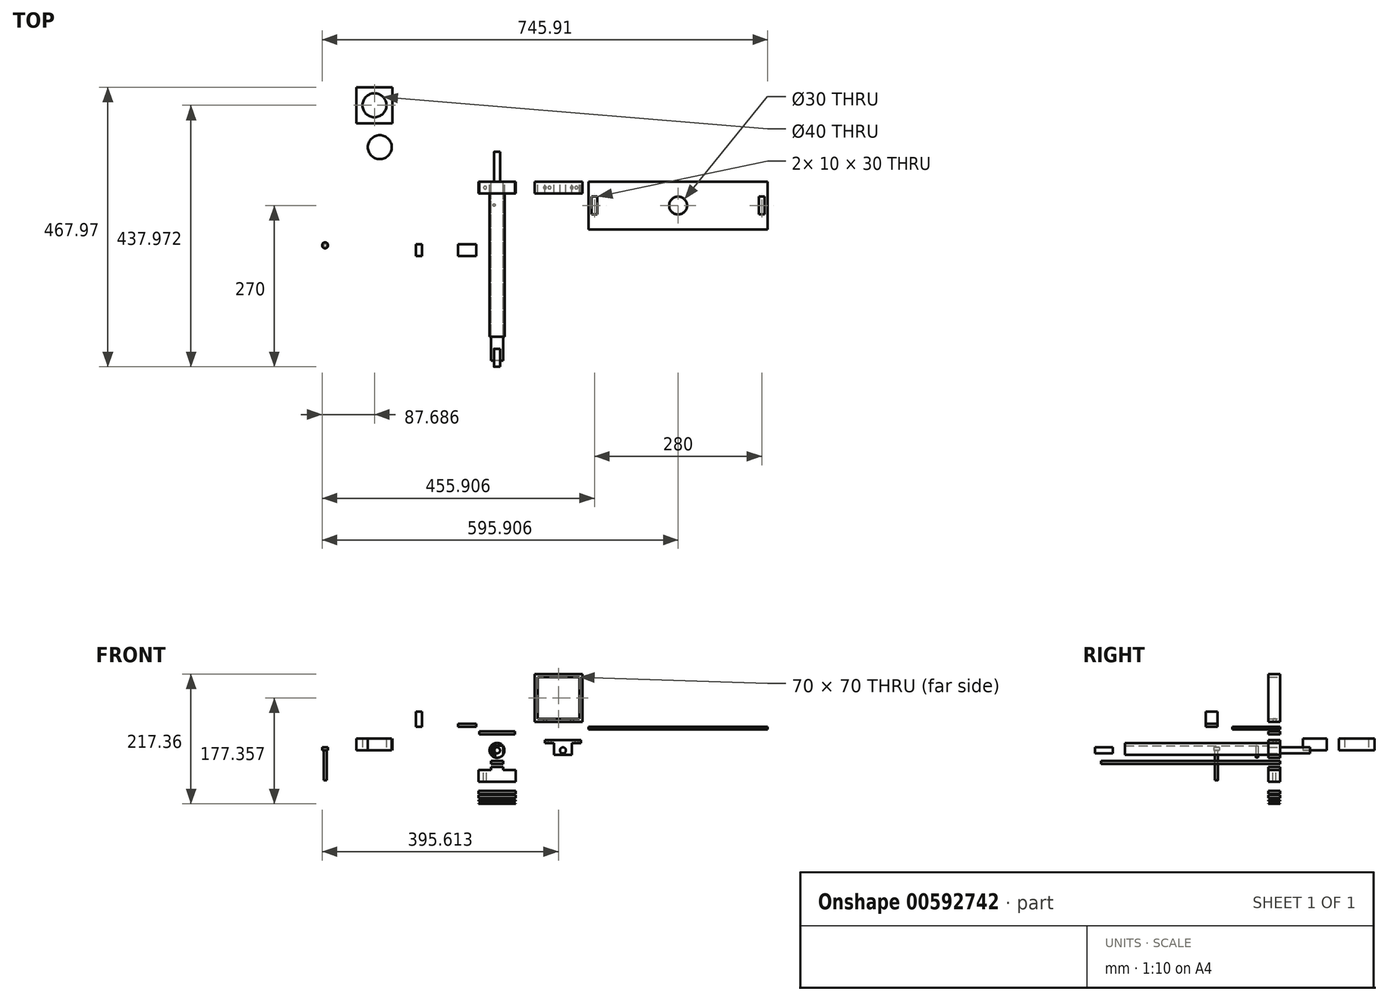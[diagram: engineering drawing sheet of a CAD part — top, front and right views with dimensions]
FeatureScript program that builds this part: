
annotation { "Feature Type Name" : "Feature", "Feature Type Description" : "" }
export const myFeature = defineFeature(function(context is Context, id is Id, definition is map)
    precondition{}
    {
        {
            var Q0;
            Q0=qCreatedBy(makeId("Front.planeOp"),FACE);
            var sketch = newSketch(context, id + "F0", { "sketchPlane" : qUnion([Q0])});
            skCircle(sketch, "E0", {"center": v(0, 0) * mm, "radius": 12.5 * mm});
            skCircle(sketch, "E1", {"center": v(110.3, 0) * mm, "radius": 5 * mm});
            skLineSegment(sketch, "E2.bottom", {"start": v(-30, 31.74) * mm, "end": v(30, 31.74) * mm});
            skLineSegment(sketch, "E2.top", {"start": v(-30, 26.74) * mm, "end": v(30, 26.74) * mm});
            skLineSegment(sketch, "E2.left", {"start": v(-30, 31.74) * mm, "end": v(-30, 26.74) * mm});
            skLineSegment(sketch, "E2.right", {"start": v(30, 31.74) * mm, "end": v(30, 26.74) * mm});
            skPoint(sketch, "E2.middle", {"position": v(0, 29.24) * mm});
            skLineSegment(sketch, "E3", {"start": v(110.3, 10) * mm, "end": v(110.3, -10) * mm, "construction": true});
            skCircle(sketch, "E4", {"center": v(110.3, 0) * mm, "radius": 12.5 * mm, "construction": true});
            skLineSegment(sketch, "E5", {"start": v(97.8, 0) * mm, "end": v(122.8, 0) * mm, "construction": true});
            skLineSegment(sketch, "E6", {"start": v(110.3, 12.5) * mm, "end": v(79.29, 12.5) * mm, "construction": true});
            skLineSegment(sketch, "E7", {"start": v(110.3, 5) * mm, "end": v(79.29, 5) * mm, "construction": true});
            skLineSegment(sketch, "E8", {"start": v(110.3, -5) * mm, "end": v(79.29, -5) * mm, "construction": true});
            skLineSegment(sketch, "E9", {"start": v(110.3, -12.5) * mm, "end": v(79.29, -12.5) * mm, "construction": true});
            skLineSegment(sketch, "E10", {"start": v(110.3, -7.5) * mm, "end": v(125.3, -7.5) * mm});
            skLineSegment(sketch, "E11", {"start": v(110.3, 17.5) * mm, "end": v(140.3, 17.5) * mm});
            skLineSegment(sketch, "E12", {"start": v(125.3, 12.5) * mm, "end": v(140.3, 12.5) * mm});
            skLineSegment(sketch, "E13", {"start": v(125.3, -7.5) * mm, "end": v(125.3, 12.5) * mm});
            skLineSegment(sketch, "E14", {"start": v(140.3, 17.5) * mm, "end": v(140.3, 12.5) * mm});
            skPoint(sketch, "E15.orphan", {"position": v(110.3, 12.5) * mm});
            skLineSegment(sketch, "E16.MirrorCS", {"start": v(95.3, 12.5) * mm, "end": v(80.3, 12.5) * mm});
            skLineSegment(sketch, "E17.MirrorCS", {"start": v(80.3, 17.5) * mm, "end": v(80.3, 12.5) * mm});
            skLineSegment(sketch, "E18.MirrorCS", {"start": v(110.3, 17.5) * mm, "end": v(80.3, 17.5) * mm});
            skLineSegment(sketch, "E19.MirrorCS", {"start": v(95.3, -7.5) * mm, "end": v(95.3, 12.5) * mm});
            skLineSegment(sketch, "E20.MirrorCS", {"start": v(110.3, -7.5) * mm, "end": v(95.3, -7.5) * mm});
            skLineSegment(sketch, "E21.top", {"start": v(0, -27.58) * mm, "end": v(10, -27.58) * mm});
            skLineSegment(sketch, "E22", {"start": v(10.93, -32.58) * mm, "end": v(30.93, -32.58) * mm});
            skLineSegment(sketch, "E23", {"start": v(30.93, -32.58) * mm, "end": v(30.93, -52.58) * mm});
            skLineSegment(sketch, "E24", {"start": v(30.93, -52.58) * mm, "end": v(0, -52.58) * mm});
            skLineSegment(sketch, "E25.MirrorCS", {"start": v(0, -27.58) * mm, "end": v(-10, -27.58) * mm});
            skLineSegment(sketch, "E26.MirrorCS", {"start": v(-10.93, -32.58) * mm, "end": v(-30.93, -32.58) * mm});
            skLineSegment(sketch, "E27.MirrorCS", {"start": v(-30.93, -32.58) * mm, "end": v(-30.93, -52.58) * mm});
            skLineSegment(sketch, "E28.MirrorCS", {"start": v(-30.93, -52.58) * mm, "end": v(0, -52.58) * mm});
            skLineSegment(sketch, "E29", {"start": v(0, -22.52) * mm, "end": v(10, -22.52) * mm});
            skLineSegment(sketch, "E30", {"start": v(10, -22.52) * mm, "end": v(10, -17.52) * mm});
            skLineSegment(sketch, "E31", {"start": v(10, -17.52) * mm, "end": v(0, -17.52) * mm});
            skLineSegment(sketch, "E32.MirrorCS", {"start": v(-10, -17.52) * mm, "end": v(0, -17.52) * mm});
            skLineSegment(sketch, "E33.MirrorCS", {"start": v(0, -22.52) * mm, "end": v(-10, -22.52) * mm});
            skLineSegment(sketch, "E34.MirrorCS", {"start": v(-10, -22.52) * mm, "end": v(-10, -17.52) * mm});
            skLineSegment(sketch, "E35.bottom", {"start": v(137.73, 52.7) * mm, "end": v(67.73, 52.7) * mm});
            skLineSegment(sketch, "E35.top", {"start": v(137.73, 122.7) * mm, "end": v(67.73, 122.7) * mm});
            skLineSegment(sketch, "E35.left", {"start": v(137.73, 52.7) * mm, "end": v(137.73, 122.7) * mm});
            skLineSegment(sketch, "E35.right", {"start": v(67.73, 52.7) * mm, "end": v(67.73, 122.7) * mm});
            skPoint(sketch, "E35.middle", {"position": v(102.73, 87.7) * mm});
            skLineSegment(sketch, "E36.bottom", {"start": v(62.73, 127.7) * mm, "end": v(142.73, 127.7) * mm});
            skLineSegment(sketch, "E36.top", {"start": v(62.73, 47.7) * mm, "end": v(142.73, 47.7) * mm});
            skLineSegment(sketch, "E36.left", {"start": v(62.73, 127.7) * mm, "end": v(62.73, 47.7) * mm});
            skLineSegment(sketch, "E36.right", {"start": v(142.73, 127.7) * mm, "end": v(142.73, 47.7) * mm});
            skLineSegment(sketch, "E37.bottom", {"start": v(-30.93, -79.86) * mm, "end": v(30.93, -79.86) * mm});
            skLineSegment(sketch, "E37.top", {"start": v(-30.93, -74.86) * mm, "end": v(30.93, -74.86) * mm});
            skLineSegment(sketch, "E37.left", {"start": v(-30.93, -79.86) * mm, "end": v(-30.93, -74.86) * mm});
            skLineSegment(sketch, "E37.right", {"start": v(30.93, -79.86) * mm, "end": v(30.93, -74.86) * mm});
            skLineSegment(sketch, "E38.MirrorCS", {"start": v(-30.74, -88.65) * mm, "end": v(31.12, -88.65) * mm});
            skLineSegment(sketch, "E39.MirrorCS", {"start": v(-30.74, -89.65) * mm, "end": v(31.12, -89.65) * mm});
            skLineSegment(sketch, "E40", {"start": v(-30.93, -82.76) * mm, "end": v(30.93, -82.76) * mm});
            skLineSegment(sketch, "E41", {"start": v(30.93, -82.76) * mm, "end": v(30.93, -84.76) * mm});
            skLineSegment(sketch, "E42", {"start": v(30.93, -84.76) * mm, "end": v(-30.93, -84.76) * mm});
            skLineSegment(sketch, "E43", {"start": v(-30.93, -84.76) * mm, "end": v(-30.93, -82.76) * mm});
            skLineSegment(sketch, "E44", {"start": v(-30.74, -88.65) * mm, "end": v(-30.74, -89.65) * mm});
            skLineSegment(sketch, "E45", {"start": v(31.12, -88.65) * mm, "end": v(31.12, -89.65) * mm});
            skLineSegment(sketch, "E46", {"start": v(-30.93, -72.74) * mm, "end": v(30.93, -72.74) * mm});
            skLineSegment(sketch, "E47", {"start": v(30.93, -72.74) * mm, "end": v(30.93, -67.74) * mm});
            skLineSegment(sketch, "E48", {"start": v(30.93, -67.74) * mm, "end": v(-30.93, -67.74) * mm});
            skLineSegment(sketch, "E49", {"start": v(-30.93, -67.74) * mm, "end": v(-30.93, -72.74) * mm});
            skLineSegment(sketch, "E50", {"start": v(-10, -27.58) * mm, "end": v(-10, -32.58) * mm});
            skLineSegment(sketch, "E51", {"start": v(-10, -32.58) * mm, "end": v(-10.93, -32.58) * mm});
            skPoint(sketch, "E52.MirrorCS.end.orphan", {"position": v(-10, -27.58) * mm});
            skPoint(sketch, "E52.MirrorCS.start.orphan", {"position": v(-10.93, -32.58) * mm});
            skLineSegment(sketch, "E53", {"start": v(10, -27.58) * mm, "end": v(10, -32.58) * mm});
            skLineSegment(sketch, "E54", {"start": v(10, -32.58) * mm, "end": v(10.93, -32.58) * mm});
            skLineSegment(sketch, "E55.left", {"start": v(194.47, 95.4) * mm, "end": v(194.47, 97.9) * mm});
            skLineSegment(sketch, "E56.bottom", {"start": v(-122.7, 157) * mm, "end": v(-422.7, 157) * mm});
            skLineSegment(sketch, "E56.top", {"start": v(-122.7, 159.5) * mm, "end": v(-422.7, 159.5) * mm});
            skLineSegment(sketch, "E56.left", {"start": v(-122.7, 157) * mm, "end": v(-122.7, 159.5) * mm});
            skLineSegment(sketch, "E56.right", {"start": v(-422.7, 157) * mm, "end": v(-422.7, 159.5) * mm});
            skLineSegment(sketch, "E57", {"start": v(-272.7, 150) * mm, "end": v(-272.7, 153.49) * mm, "construction": true});
            skPoint(sketch, "E57.startSnap0", {"position": v(-272.7, 157) * mm});
            skSolve(sketch);
        }
        {
            var Q0;
            Q0=makeQuery(id+"F0.imprint","IMPRINT",FACE,{"disambiguationData":[TD([[makeQuery(id+"F0.imprint","IMPRINT",EDGE,{"derivedFrom":sQuery(id+"F0.wireOp",EDGE,"E1")}),-1.0]])]});
            var Q1;
            Q1=makeQuery(id+"F0.imprint","IMPRINT",FACE,{"disambiguationData":[TD([[makeQuery(id+"F0.imprint","IMPRINT",EDGE,{"derivedFrom":sQuery(id+"F0.wireOp",EDGE,"E2.bottom")}),-1.0]])]});
            var Q2;
            Q2=makeQuery(id+"F0.imprint","IMPRINT",FACE,{"disambiguationData":[TD([[makeQuery(id+"F0.imprint","IMPRINT",EDGE,{"derivedFrom":sQuery(id+"F0.wireOp",EDGE,"E21.top")}),-1.0]])]});
            var Q3;
            Q3=makeQuery(id+"F0.imprint","IMPRINT",FACE,{"disambiguationData":[TD([[makeQuery(id+"F0.imprint","IMPRINT",EDGE,{"derivedFrom":sQuery(id+"F0.wireOp",EDGE,"E35.bottom")}),1.0]])]});
            var Q4;
            Q4=makeQuery(id+"F0.imprint","IMPRINT",FACE,{"disambiguationData":[TD([[makeQuery(id+"F0.imprint","IMPRINT",EDGE,{"derivedFrom":sQuery(id+"F0.wireOp",EDGE,"E37.bottom")}),1.0]])]});
            var Q5;
            Q5=makeQuery(id+"F0.imprint","IMPRINT",FACE,{"disambiguationData":[TD([[makeQuery(id+"F0.imprint","IMPRINT",EDGE,{"derivedFrom":sQuery(id+"F0.wireOp",EDGE,"E38.MirrorCS")}),-1.0]])]});
            var Q6;
            Q6=makeQuery(id+"F0.imprint","IMPRINT",FACE,{"disambiguationData":[TD([[makeQuery(id+"F0.imprint","IMPRINT",EDGE,{"derivedFrom":sQuery(id+"F0.wireOp",EDGE,"E40")}),-1.0]])]});
            var Q7;
            Q7=makeQuery(id+"F0.imprint","IMPRINT",FACE,{"disambiguationData":[TD([[makeQuery(id+"F0.imprint","IMPRINT",EDGE,{"derivedFrom":sQuery(id+"F0.wireOp",EDGE,"E46")}),1.0]])]});
            var Q8;
            {var subQ5=sQuery(id+"F0.wireOp",EDGE,"E55.right");Q8=makeQuery(id+"F0.imprint","IMPRINT",FACE,{"disambiguationData":[TD([[makeQuery(id+"F0.imprint","IMPRINT",EDGE,{"derivedFrom":subQ5}),-1.0]])]});}
            extrude(context, id + "F1", {"entities" : qUnion([Q0, Q1, Q2, Q3, Q4, Q5, Q6, Q7, Q8]), "depth" : 20 * mm, "offsetDistance" : 25 * mm});
        }
        {
            var Q0;
            Q0=makeQuery(id+"F0.imprint","IMPRINT",FACE,{"disambiguationData":[TD([[makeQuery(id+"F0.imprint","IMPRINT",EDGE,{"derivedFrom":sQuery(id+"F0.wireOp",EDGE,"E0")}),1.0]])]});
            extrude(context, id + "F2", {"entities" : qUnion([Q0]), "depth" : 260 * mm, "offsetDistance" : 25 * mm});
        }
        {
            var Q0;
            Q0=makeQuery(id+"F2.opExtrude","CAP_FACE",FACE,{"disambiguationData":[OSD([sQuery(id+"F0.wireOp",EDGE,"E0")])],"isStart":false});
            var sketch = newSketch(context, id + "F3", { "sketchPlane" : qUnion([Q0])});
            skCircle(sketch, "E58", {"center": v(0, 0) * mm, "radius": 5 * mm});
            skSolve(sketch);
        }
        {
            var Q0;
            Q0=makeQuery(id+"F3.imprint","IMPRINT",FACE,{"disambiguationData":[TD([[makeQuery(id+"F3.imprint","IMPRINT",EDGE,{"derivedFrom":sQuery(id+"F3.wireOp",EDGE,"E58")}),1.0]])]});
            extrude(context, id + "F4", {"entities" : qUnion([Q0]), "operationType" : NewBodyOperationType.ADD, "depth" : 50 * mm, "offsetDistance" : 25 * mm});
        }
        {
            var Q0;
            Q0=makeQuery(id+"F0.imprint","IMPRINT",FACE,{"disambiguationData":[TD([[makeQuery(id+"F0.imprint","IMPRINT",EDGE,{"derivedFrom":sQuery(id+"F0.wireOp",EDGE,"E29")}),1.0]])]});
            extrude(context, id + "F5", {"entities" : qUnion([Q0]), "depth" : 300 * mm, "offsetDistance" : 25 * mm});
        }
        {
            var Q0;
            Q0=makeQuery(id+"F1.opExtrude","SWEPT_FACE",FACE,{"disambiguationData":[OSD([sQuery(id+"F0.wireOp",EDGE,"E26.MirrorCS")])]});
            var sketch = newSketch(context, id + "F6", { "sketchPlane" : qUnion([Q0])});
            skCircle(sketch, "E59", {"center": v(-20, -10) * mm, "radius": 2.5 * mm});
            skSolve(sketch);
        }
        {
            var Q0;
            Q0=makeQuery(id+"F6.imprint","IMPRINT",FACE,{"disambiguationData":[TD([[makeQuery(id+"F6.imprint","IMPRINT",EDGE,{"derivedFrom":sQuery(id+"F6.wireOp",EDGE,"E59")}),1.0]])]});
            var Q1;
            Q1=makeQuery(id+"FNYWGUJzlf6PVvf_4.imprint","IMPRINT",FACE,{"disambiguationData":[TD([[makeQuery(id+"FNYWGUJzlf6PVvf_4.imprint","IMPRINT",EDGE,{"derivedFrom":sQuery(id+"FNYWGUJzlf6PVvf_4.wireOp",EDGE,"JrdPBHnR-5tIZ-cZ5f-IPz8-CMVoVNEgzM20")}),1.0]])]});
            extrude(context, id + "F7", {"entities" : qUnion([Q0, Q1]), "operationType" : NewBodyOperationType.REMOVE, "oppositeDirection" : true, "depth" : 25 * mm, "offsetDistance" : 25 * mm});
        }
        {
            var Q0;
            Q0=makeQuery(id+"F1.opExtrude","SWEPT_FACE",FACE,{"disambiguationData":[OSD([sQuery(id+"F0.wireOp",EDGE,"E12")])]});
            var sketch = newSketch(context, id + "F8", { "sketchPlane" : qUnion([Q0])});
            skCircle(sketch, "E60", {"center": v(132.8, 10) * mm, "radius": 2.5 * mm});
            skPoint(sketch, "E60.centerSnap0", {"position": v(132.8, 20) * mm});
            skPoint(sketch, "E60.centerSnap1", {"position": v(125.3, 10) * mm});
            skSolve(sketch);
        }
        {
            var Q0;
            Q0=makeQuery(id+"F1.opExtrude","SWEPT_FACE",FACE,{"disambiguationData":[OSD([sQuery(id+"F0.wireOp",EDGE,"E16.MirrorCS")])]});
            var sketch = newSketch(context, id + "F9", { "sketchPlane" : qUnion([Q0])});
            skCircle(sketch, "E61", {"center": v(87.8, 10) * mm, "radius": 2.5 * mm});
            skPoint(sketch, "E61.centerSnap0", {"position": v(80.3, 10) * mm});
            skPoint(sketch, "E61.centerSnap1", {"position": v(87.8, 20) * mm});
            skSolve(sketch);
        }
        {
            var Q0;
            Q0=makeQuery(id+"F9.imprint","IMPRINT",FACE,{"disambiguationData":[TD([[makeQuery(id+"F9.imprint","IMPRINT",EDGE,{"derivedFrom":sQuery(id+"F9.wireOp",EDGE,"E61")}),1.0]])]});
            var Q1;
            Q1=makeQuery(id+"F8.imprint","IMPRINT",FACE,{"disambiguationData":[TD([[makeQuery(id+"F8.imprint","IMPRINT",EDGE,{"derivedFrom":sQuery(id+"F8.wireOp",EDGE,"E60")}),1.0]])]});
            extrude(context, id + "F10", {"entities" : qUnion([Q0, Q1]), "operationType" : NewBodyOperationType.REMOVE, "oppositeDirection" : true, "depth" : 25 * mm, "offsetDistance" : 25 * mm});
        }
        {
            var Q0;
            Q0=makeQuery(id+"F5.opExtrude","SWEPT_FACE",FACE,{"disambiguationData":[OSD([sQuery(id+"F0.wireOp",EDGE,"E31"),sQuery(id+"F0.wireOp",EDGE,"E32.MirrorCS")])]});
            var sketch = newSketch(context, id + "F11", { "sketchPlane" : qUnion([Q0])});
            skLineSegment(sketch, "E62", {"start": v(-10, -280) * mm, "end": v(10, -280) * mm});
            skCircle(sketch, "E63", {"center": v(5, -39.13) * mm, "radius": 1.93 * mm});
            skPoint(sketch, "E64.orphan", {"position": v(0, -300) * mm});
            skCircle(sketch, "E65.MirrorC", {"center": v(-5, -39.13) * mm, "radius": 1.93 * mm});
            skLineSegment(sketch, "E66", {"start": v(10, -20) * mm, "end": v(-10, -20) * mm});
            skSolve(sketch);
        }
        {
            var Q0;
            Q0=makeQuery(id+"F11.imprint","IMPRINT",FACE,{"disambiguationData":[TD([[makeQuery(id+"F11.imprint","IMPRINT",EDGE,{"derivedFrom":sQuery(id+"F11.wireOp",EDGE,"E65.MirrorC")}),-1.0]])]});
            var Q1;
            Q1=makeQuery(id+"F11.imprint","IMPRINT",FACE,{"disambiguationData":[TD([[makeQuery(id+"F11.imprint","IMPRINT",EDGE,{"derivedFrom":sQuery(id+"F11.wireOp",EDGE,"E63")}),1.0]])]});
            extrude(context, id + "F12", {"entities" : qUnion([Q0, Q1]), "operationType" : NewBodyOperationType.REMOVE, "depth" : 25 * mm, "offsetDistance" : 25 * mm});
        }
        {
            var Q0;
            Q0=makeQuery(id+"F1.opExtrude","SWEPT_FACE",FACE,{"disambiguationData":[OSD([sQuery(id+"F0.wireOp",EDGE,"E36.top")])]});
            var sketch = newSketch(context, id + "F13", { "sketchPlane" : qUnion([Q0])});
            skCircle(sketch, "E67", {"center": v(80.23, 10) * mm, "radius": 2.5 * mm});
            skCircle(sketch, "E68", {"center": v(125.23, 10) * mm, "radius": 2.5 * mm});
            skLineSegment(sketch, "E69", {"start": v(62.73, 20) * mm, "end": v(142.73, 20) * mm, "construction": true});
            skLineSegment(sketch, "E70", {"start": v(142.73, 20) * mm, "end": v(142.73, 0) * mm, "construction": true});
            skLineSegment(sketch, "E71", {"start": v(142.73, 0) * mm, "end": v(62.73, 0) * mm, "construction": true});
            skLineSegment(sketch, "E72", {"start": v(62.73, 0) * mm, "end": v(62.73, 20) * mm, "construction": true});
            skLineSegment(sketch, "E73", {"start": v(67.73, 20) * mm, "end": v(67.73, 0) * mm, "construction": true});
            skLineSegment(sketch, "E74", {"start": v(137.73, 20) * mm, "end": v(137.73, 0) * mm, "construction": true});
            skSolve(sketch);
        }
        {
            var Q0;
            Q0=makeQuery(id+"F2.opExtrude","CAP_FACE",FACE,{"disambiguationData":[OSD([sQuery(id+"F0.wireOp",EDGE,"E0")])],"isStart":true});
            var sketch = newSketch(context, id + "F14", { "sketchPlane" : qUnion([Q0])});
            skCircle(sketch, "E75", {"center": v(0, 0) * mm, "radius": 5 * mm});
            skSolve(sketch);
        }
        {
            var Q0;
            Q0=qSketchRegion(id+"F14",true);
            extrude(context, id + "F15", {"entities" : qUnion([Q0]), "operationType" : NewBodyOperationType.ADD, "depth" : 50 * mm, "offsetDistance" : 25 * mm});
        }
        {
            var Q0;
            Q0=qCreatedBy(makeId("Front.planeOp"),FACE);
            var sketch = newSketch(context, id + "F16", { "sketchPlane" : qUnion([Q0])});
            skLineSegment(sketch, "E76.bottom", {"start": v(153.03, 39.78) * mm, "end": v(453.03, 39.78) * mm});
            skLineSegment(sketch, "E76.top", {"start": v(153.03, 34.78) * mm, "end": v(453.03, 34.78) * mm});
            skLineSegment(sketch, "E76.left", {"start": v(153.03, 39.78) * mm, "end": v(153.03, 34.78) * mm});
            skLineSegment(sketch, "E76.right", {"start": v(453.03, 39.78) * mm, "end": v(453.03, 34.78) * mm});
            skSolve(sketch);
        }
        {
            var Q0;
            Q0=makeQuery(id+"F16.imprint","IMPRINT",FACE,{"disambiguationData":[TD([[makeQuery(id+"F16.imprint","IMPRINT",EDGE,{"derivedFrom":sQuery(id+"F16.wireOp",EDGE,"E76.bottom")}),-1.0]])]});
            extrude(context, id + "F17", {"entities" : qUnion([Q0]), "depth" : 80 * mm, "offsetDistance" : 25 * mm});
        }
        {
            var Q0;
            Q0=makeQuery(id+"F17.opExtrude","SWEPT_FACE",FACE,{"disambiguationData":[OSD([sQuery(id+"F16.wireOp",EDGE,"E76.bottom")])]});
            var sketch = newSketch(context, id + "F18", { "sketchPlane" : qUnion([Q0])});
            skLineSegment(sketch, "E77", {"start": v(173.03, 0) * mm, "end": v(173.03, -80) * mm});
            skLineSegment(sketch, "E78.bottom", {"start": v(158.03, -25) * mm, "end": v(168.03, -25) * mm});
            skLineSegment(sketch, "E78.top", {"start": v(158.03, -55) * mm, "end": v(168.03, -55) * mm});
            skLineSegment(sketch, "E78.left", {"start": v(158.03, -25) * mm, "end": v(158.03, -55) * mm});
            skLineSegment(sketch, "E78.right", {"start": v(168.03, -25) * mm, "end": v(168.03, -55) * mm});
            skPoint(sketch, "E78.middle", {"position": v(163.03, -40) * mm});
            skLineSegment(sketch, "E79", {"start": v(303.03, 0) * mm, "end": v(303.03, -80) * mm, "construction": true});
            skLineSegment(sketch, "E80.MirrorCS", {"start": v(438.03, -25) * mm, "end": v(438.03, -55) * mm});
            skLineSegment(sketch, "E81.MirrorCS", {"start": v(448.03, -25) * mm, "end": v(438.03, -25) * mm});
            skLineSegment(sketch, "E82.MirrorCS", {"start": v(448.03, -25) * mm, "end": v(448.03, -55) * mm});
            skLineSegment(sketch, "E83.MirrorCS", {"start": v(448.03, -55) * mm, "end": v(438.03, -55) * mm});
            skLineSegment(sketch, "E84.MirrorCS", {"start": v(433.03, 0) * mm, "end": v(433.03, -80) * mm});
            skLineSegment(sketch, "E85.bottom", {"start": v(-65.07, -104.85) * mm, "end": v(-35.07, -104.85) * mm});
            skLineSegment(sketch, "E85.top", {"start": v(-65.07, -124.85) * mm, "end": v(-35.07, -124.85) * mm});
            skLineSegment(sketch, "E85.left", {"start": v(-65.07, -104.85) * mm, "end": v(-65.07, -124.85) * mm});
            skLineSegment(sketch, "E85.right", {"start": v(-35.07, -104.85) * mm, "end": v(-35.07, -124.85) * mm});
            skLineSegment(sketch, "E86.bottom", {"start": v(-135.53, -104.85) * mm, "end": v(-125.53, -104.85) * mm});
            skLineSegment(sketch, "E86.top", {"start": v(-135.53, -124.85) * mm, "end": v(-125.53, -124.85) * mm});
            skLineSegment(sketch, "E86.left", {"start": v(-135.53, -104.85) * mm, "end": v(-135.53, -124.85) * mm});
            skLineSegment(sketch, "E86.right", {"start": v(-125.53, -104.85) * mm, "end": v(-125.53, -124.85) * mm});
            skCircle(sketch, "E87", {"center": v(303.03, -40) * mm, "radius": 15 * mm});
            skSolve(sketch);
        }
        {
            var Q0;
            Q0=qCreatedBy(makeId("Top.planeOp"),FACE);
            var sketch = newSketch(context, id + "F19", { "sketchPlane" : qUnion([Q0])});
            skCircle(sketch, "E88", {"center": v(-196.25, 57.8) * mm, "radius": 20 * mm});
            skLineSegment(sketch, "E89.bottom", {"start": v(-235.2, 97.97) * mm, "end": v(-175.2, 97.97) * mm});
            skLineSegment(sketch, "E89.top", {"start": v(-235.2, 157.97) * mm, "end": v(-175.2, 157.97) * mm});
            skLineSegment(sketch, "E89.left", {"start": v(-235.2, 97.97) * mm, "end": v(-235.2, 157.97) * mm});
            skLineSegment(sketch, "E89.right", {"start": v(-175.2, 97.97) * mm, "end": v(-175.2, 157.97) * mm});
            skCircle(sketch, "E90", {"center": v(-205.2, 127.97) * mm, "radius": 20 * mm});
            skPoint(sketch, "E90.centerSnap0", {"position": v(-175.2, 127.97) * mm});
            skPoint(sketch, "E90.centerSnap1", {"position": v(-205.2, 97.97) * mm});
            skSolve(sketch);
        }
        {
            var Q0;
            Q0=makeQuery(id+"F19.imprint","IMPRINT",FACE,{"disambiguationData":[TD([[makeQuery(id+"F19.imprint","IMPRINT",EDGE,{"derivedFrom":sQuery(id+"F19.wireOp",EDGE,"E88")}),1.0]])]});
            extrude(context, id + "F20", {"entities" : qUnion([Q0]), "depth" : 20 * mm, "offsetDistance" : 25 * mm});
        }
        {
            var Q0;
            Q0=makeQuery(id+"F19.imprint","IMPRINT",FACE,{"disambiguationData":[TD([[makeQuery(id+"F19.imprint","IMPRINT",EDGE,{"derivedFrom":sQuery(id+"F19.wireOp",EDGE,"E89.bottom")}),1.0]])]});
            extrude(context, id + "F21", {"entities" : qUnion([Q0]), "depth" : 20 * mm, "offsetDistance" : 25 * mm});
        }
        {
            var Q0;
            Q0=makeQuery(id+"F18.imprint","IMPRINT",FACE,{"disambiguationData":[TD([[makeQuery(id+"F18.imprint","IMPRINT",EDGE,{"derivedFrom":sQuery(id+"F18.wireOp",EDGE,"E78.bottom")}),-1.0]])]});
            var Q1;
            Q1=makeQuery(id+"F18.imprint","IMPRINT",FACE,{"disambiguationData":[TD([[makeQuery(id+"F18.imprint","IMPRINT",EDGE,{"derivedFrom":sQuery(id+"F18.wireOp",EDGE,"E80.MirrorCS")}),1.0]])]});
            var Q2;
            Q2=makeQuery(id+"F18.imprint","IMPRINT",FACE,{"disambiguationData":[TD([[makeQuery(id+"F18.imprint","IMPRINT",EDGE,{"derivedFrom":sQuery(id+"F18.wireOp",EDGE,"E87")}),1.0]])]});
            extrude(context, id + "F22", {"entities" : qUnion([Q0, Q1, Q2]), "operationType" : NewBodyOperationType.REMOVE, "endBound" : BoundingType.THROUGH_ALL, "oppositeDirection" : true, "depth" : 25 * mm, "offsetDistance" : 25 * mm});
        }
        {
            var Q0;
            Q0=makeQuery(id+"F18.imprint","IMPRINT",FACE,{"disambiguationData":[TD([[makeQuery(id+"F18.imprint","IMPRINT",EDGE,{"derivedFrom":sQuery(id+"F18.wireOp",EDGE,"E86.bottom")}),-1.0]])]});
            extrude(context, id + "F23", {"entities" : qUnion([Q0]), "depth" : 25 * mm, "offsetDistance" : 25 * mm});
        }
        {
            var Q0;
            Q0=makeQuery(id+"F18.imprint","IMPRINT",FACE,{"disambiguationData":[TD([[makeQuery(id+"F18.imprint","IMPRINT",EDGE,{"derivedFrom":sQuery(id+"F18.wireOp",EDGE,"E85.bottom")}),-1.0]])]});
            extrude(context, id + "F24", {"entities" : qUnion([Q0]), "depth" : 5 * mm, "offsetDistance" : 25 * mm});
        }
        {
            var Q0;
            Q0=makeQuery(id+"F13.imprint","IMPRINT",FACE,{"disambiguationData":[TD([[makeQuery(id+"F13.imprint","IMPRINT",EDGE,{"derivedFrom":sQuery(id+"F13.wireOp",EDGE,"E68")}),1.0]])]});
            var Q1;
            Q1=makeQuery(id+"F13.imprint","IMPRINT",FACE,{"disambiguationData":[TD([[makeQuery(id+"F13.imprint","IMPRINT",EDGE,{"derivedFrom":sQuery(id+"F13.wireOp",EDGE,"E67")}),1.0]])]});
            extrude(context, id + "F25", {"entities" : qUnion([Q0, Q1]), "operationType" : NewBodyOperationType.REMOVE, "endBound" : BoundingType.UP_TO_NEXT, "oppositeDirection" : true, "depth" : 25 * mm, "offsetDistance" : 25 * mm});
        }
        {
            var Q0;
            Q0=qCreatedBy(makeId("Top.planeOp"),FACE);
            var sketch = newSketch(context, id + "F26", { "sketchPlane" : qUnion([Q0])});
            skCircle(sketch, "E91", {"center": v(-287.88, -106.71) * mm, "radius": 5 * mm});
            skSolve(sketch);
        }
        {
            var Q0;
            Q0=makeQuery(id+"F26.imprint","IMPRINT",FACE,{"disambiguationData":[TD([[makeQuery(id+"F26.imprint","IMPRINT",EDGE,{"derivedFrom":sQuery(id+"F26.wireOp",EDGE,"E91")}),1.0]])]});
            extrude(context, id + "F27", {"entities" : qUnion([Q0]), "depth" : 5 * mm, "offsetDistance" : 25 * mm});
        }
        {
            var Q0;
            Q0=makeQuery(id+"F26.imprint","IMPRINT",FACE,{"disambiguationData":[TD([[makeQuery(id+"F26.imprint","IMPRINT",EDGE,{"derivedFrom":sQuery(id+"F26.wireOp",EDGE,"E91")}),1.0]])]});
            var sketch = newSketch(context, id + "F28", { "sketchPlane" : qUnion([Q0])});
            skCircle(sketch, "E92", {"center": v(-287.73, -106.85) * mm, "radius": 2.5 * mm});
            skSolve(sketch);
        }
        {
            var Q0;
            Q0=makeQuery(id+"F28.imprint","IMPRINT",FACE,{"disambiguationData":[TD([[makeQuery(id+"F28.imprint","IMPRINT",EDGE,{"derivedFrom":sQuery(id+"F28.wireOp",EDGE,"E92")}),1.0]])]});
            extrude(context, id + "F29", {"entities" : qUnion([Q0]), "operationType" : NewBodyOperationType.ADD, "oppositeDirection" : true, "depth" : 50 * mm, "offsetDistance" : 25 * mm});
        }
    });
